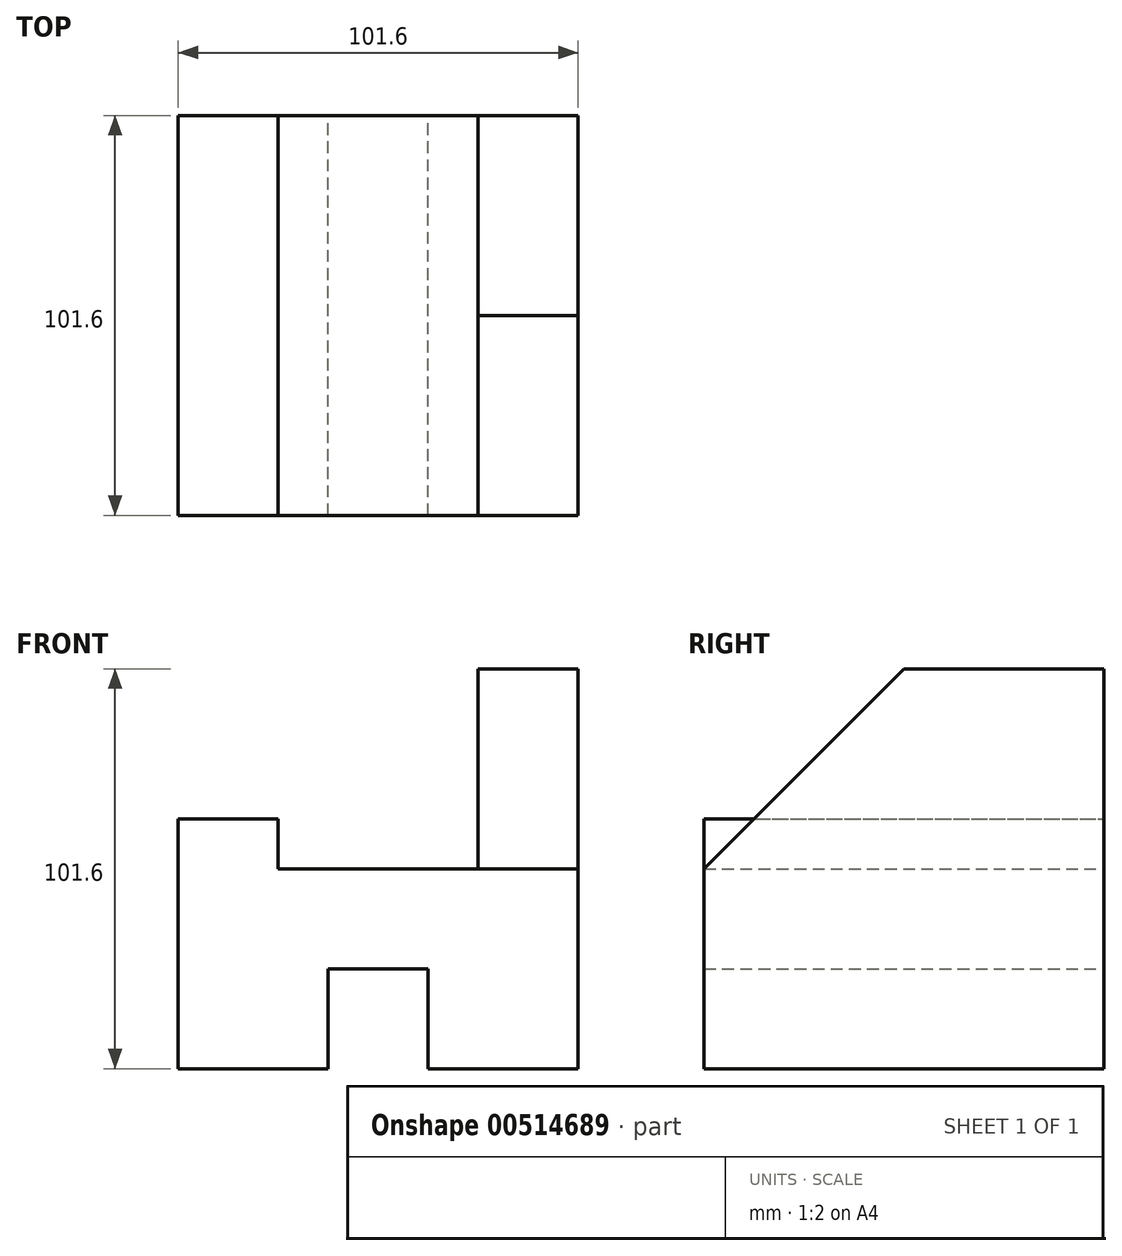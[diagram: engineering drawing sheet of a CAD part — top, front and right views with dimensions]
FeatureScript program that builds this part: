
annotation { "Feature Type Name" : "Feature", "Feature Type Description" : "" }
export const myFeature = defineFeature(function(context is Context, id is Id, definition is map)
    precondition{}
    {
        {
            var Q0;
            Q0=qCreatedBy(makeId("Front.planeOp"),FACE);
            var sketch = newSketch(context, id + "F0", { "sketchPlane" : qUnion([Q0])});
            skLineSegment(sketch, "E0", {"start": v(-61.72, -43.14) * mm, "end": v(-23.62, -43.14) * mm});
            skLineSegment(sketch, "E1", {"start": v(-23.62, -43.14) * mm, "end": v(-23.62, -17.74) * mm});
            skLineSegment(sketch, "E2", {"start": v(-23.62, -17.74) * mm, "end": v(1.78, -17.74) * mm});
            skLineSegment(sketch, "E3", {"start": v(1.78, -17.74) * mm, "end": v(1.78, -43.14) * mm});
            skLineSegment(sketch, "E4", {"start": v(1.78, -43.14) * mm, "end": v(39.88, -43.14) * mm});
            skLineSegment(sketch, "E5", {"start": v(-61.72, -43.14) * mm, "end": v(-61.72, 20.36) * mm});
            skLineSegment(sketch, "E6", {"start": v(39.88, -43.14) * mm, "end": v(39.88, 58.46) * mm});
            skLineSegment(sketch, "E7", {"start": v(-61.72, 20.36) * mm, "end": v(-36.32, 20.36) * mm});
            skLineSegment(sketch, "E8", {"start": v(-36.32, 20.36) * mm, "end": v(-36.32, 7.66) * mm});
            skLineSegment(sketch, "E9", {"start": v(-36.32, 7.66) * mm, "end": v(14.48, 7.66) * mm});
            skLineSegment(sketch, "E10", {"start": v(14.48, 7.66) * mm, "end": v(14.48, 58.46) * mm});
            skLineSegment(sketch, "E11", {"start": v(14.48, 58.46) * mm, "end": v(39.88, 58.46) * mm});
            skSolve(sketch);
        }
        {
            var Q0;
            Q0=makeQuery(id+"F0.imprint","IMPRINT",FACE,{"disambiguationData":[TD([[makeQuery(id+"F0.imprint","IMPRINT",EDGE,{"derivedFrom":sQuery(id+"F0.wireOp",EDGE,"E0")}),1.0]])]});
            extrude(context, id + "F1", {"entities" : qUnion([Q0]), "depth" : 101.6 * mm, "offsetDistance" : 25.4 * mm});
        }
        {
            var Q0;
            Q0=makeQuery(id+"F1.opExtrude","SWEPT_FACE",FACE,{"disambiguationData":[OSD([sQuery(id+"F0.wireOp",EDGE,"E6")])]});
            var sketch = newSketch(context, id + "F2", { "sketchPlane" : qUnion([Q0])});
            skLineSegment(sketch, "E12", {"start": v(-101.6, 58.46) * mm, "end": v(-101.6, 7.66) * mm});
            skLineSegment(sketch, "E13", {"start": v(-101.6, 58.46) * mm, "end": v(-50.8, 58.46) * mm});
            skLineSegment(sketch, "E14", {"start": v(-101.6, 7.66) * mm, "end": v(-50.8, 58.46) * mm});
            skSolve(sketch);
        }
        {
            var Q0;
            Q0=makeQuery(id+"F2.imprint","IMPRINT",FACE,{"disambiguationData":[TD([[makeQuery(id+"F2.imprint","IMPRINT",EDGE,{"derivedFrom":sQuery(id+"F2.wireOp",EDGE,"E12")}),-1.0]])]});
            extrude(context, id + "F3", {"entities" : qUnion([Q0]), "operationType" : NewBodyOperationType.REMOVE, "oppositeDirection" : true, "depth" : 50.8 * mm, "offsetDistance" : 25.4 * mm});
        }
    });
